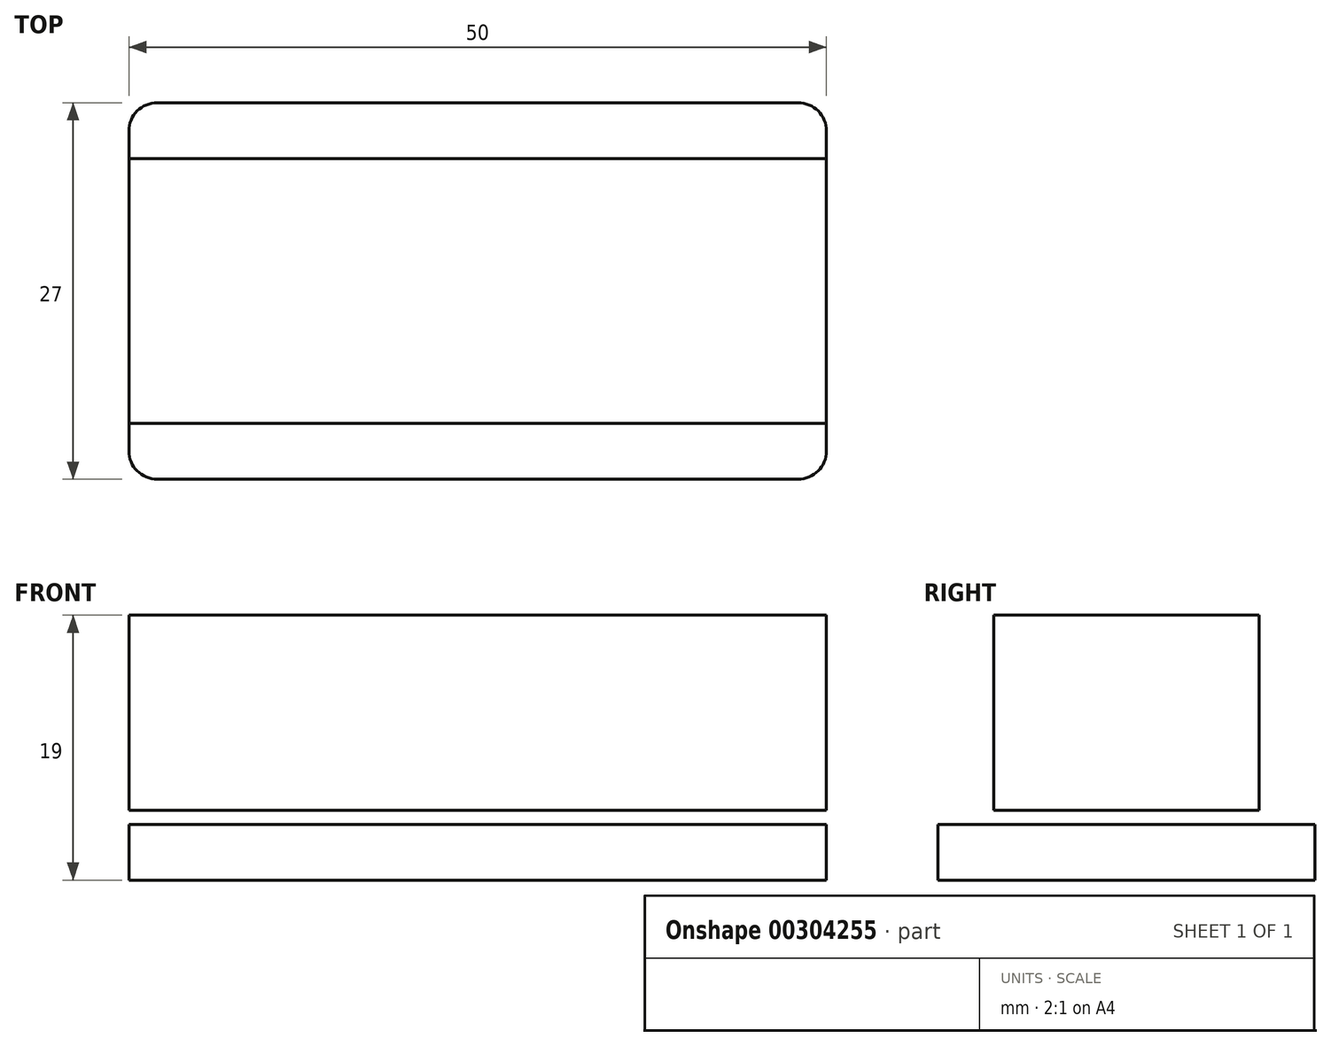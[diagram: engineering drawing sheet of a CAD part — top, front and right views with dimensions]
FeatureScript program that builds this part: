
annotation { "Feature Type Name" : "Feature", "Feature Type Description" : "" }
export const myFeature = defineFeature(function(context is Context, id is Id, definition is map)
    precondition{}
    {
        {
            var Q0;
            Q0=qCreatedBy(makeId("Top.planeOp"),FACE);
            var sketch = newSketch(context, id + "F0", { "sketchPlane" : qUnion([Q0])});
            skLineSegment(sketch, "E0.bottom", {"start": v(22.97, 13.5) * mm, "end": v(-22.97, 13.5) * mm});
            skLineSegment(sketch, "E0.top", {"start": v(22.97, -13.5) * mm, "end": v(-22.97, -13.5) * mm});
            skLineSegment(sketch, "E0.left", {"start": v(25, 11.47) * mm, "end": v(25, -11.47) * mm});
            skLineSegment(sketch, "E0.right", {"start": v(-25, 11.47) * mm, "end": v(-25, -11.47) * mm});
            skPoint(sketch, "E0.middle", {"position": v(0, 0) * mm});
            skPoint(sketch, "E1.visualSharp", {"position": v(-25, 13.5) * mm});
            skArc(sketch, "E1.filletArc", {"start": v(-22.97, 13.5) * mm, "mid": v(-24.4, 12.9) * mm, "end": v(-25, 11.47) * mm});
            skPoint(sketch, "E2.visualSharp", {"position": v(-25, -13.5) * mm});
            skArc(sketch, "E2.filletArc", {"start": v(-25, -11.47) * mm, "mid": v(-24.4, -12.9) * mm, "end": v(-22.97, -13.5) * mm});
            skPoint(sketch, "E3.visualSharp", {"position": v(25, -13.5) * mm});
            skArc(sketch, "E3.filletArc", {"start": v(22.97, -13.5) * mm, "mid": v(24.4, -12.9) * mm, "end": v(25, -11.47) * mm});
            skPoint(sketch, "E4.visualSharp", {"position": v(25, 13.5) * mm});
            skArc(sketch, "E4.filletArc", {"start": v(25, 11.47) * mm, "mid": v(24.4, 12.9) * mm, "end": v(22.97, 13.5) * mm});
            skSolve(sketch);
        }
        {
            var Q0;
            Q0=makeQuery(id+"F0.imprint","IMPRINT",FACE,{"disambiguationData":[TD([[makeQuery(id+"F0.imprint","IMPRINT",EDGE,{"derivedFrom":sQuery(id+"F0.wireOp",EDGE,"E0.bottom")}),1.0]])]});
            extrude(context, id + "F1", {"entities" : qUnion([Q0]), "depth" : 4 * mm});
        }
        {
            var Q0;
            Q0=makeQuery(id+"F1.opExtrude","CAP_FACE",FACE,{"disambiguationData":[OSD([sQuery(id+"F0.wireOp",EDGE,"E0.bottom"),sQuery(id+"F0.wireOp",EDGE,"E0.top"),sQuery(id+"F0.wireOp",EDGE,"E0.left"),sQuery(id+"F0.wireOp",EDGE,"E0.right"),sQuery(id+"F0.wireOp",EDGE,"E1.filletArc"),sQuery(id+"F0.wireOp",EDGE,"E2.filletArc"),sQuery(id+"F0.wireOp",EDGE,"E3.filletArc"),sQuery(id+"F0.wireOp",EDGE,"E4.filletArc")])],"isStart":false});
            var sketch = newSketch(context, id + "F2", { "sketchPlane" : qUnion([Q0])});
            skLineSegment(sketch, "E5.bottom", {"start": v(25, -9.5) * mm, "end": v(-25, -9.5) * mm});
            skLineSegment(sketch, "E5.top", {"start": v(25, 9.5) * mm, "end": v(-25, 9.5) * mm});
            skLineSegment(sketch, "E5.left", {"start": v(25, -9.5) * mm, "end": v(25, 9.5) * mm});
            skLineSegment(sketch, "E5.right", {"start": v(-25, -9.5) * mm, "end": v(-25, 9.5) * mm});
            skPoint(sketch, "E5.middle", {"position": v(0, 0) * mm});
            skSolve(sketch);
        }
        {
            var Q0;
            Q0=makeQuery(id+"F2.imprint","IMPRINT",FACE,{"disambiguationData":[TD([[makeQuery(id+"F2.imprint","IMPRINT",EDGE,{"derivedFrom":sQuery(id+"F2.wireOp",EDGE,"E5.bottom")}),-1.0]])]});
            extrude(context, id + "F3", {"entities" : qUnion([Q0]), "depth" : 14 * mm});
        }
        {
            var Q0;
            Q0=makeQuery(id+"F3.opExtrude","SWEPT_BODY",BODY,{"disambiguationData":[OSD([sQuery(id+"F2.wireOp",EDGE,"E5.bottom"),sQuery(id+"F2.wireOp",EDGE,"E5.top"),sQuery(id+"F2.wireOp",EDGE,"E5.left"),sQuery(id+"F2.wireOp",EDGE,"E5.right")])]});
            transform(context, id + "F4", {"entities" : qUnion([Q0]), "transformType" : TransformType.TRANSLATION_3D, "dx" : 0 * mm, "dy" : 0 * mm, "dz" : 1 * mm, "makeCopy" : false});
        }
    });
